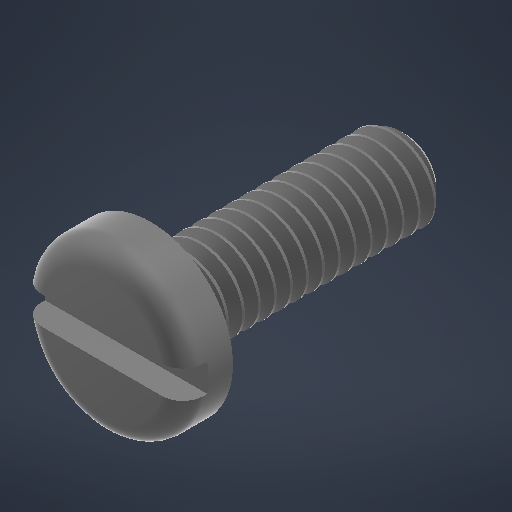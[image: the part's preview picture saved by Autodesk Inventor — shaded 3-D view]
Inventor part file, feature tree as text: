
AUTODESK INVENTOR PART (.ipt)
format: ipt  version: 2025.2 (Build 292293000, 293)  size: 487,424 bytes
history: native  units: in
note: dims shown in document units (in); Inventor stores cm internally (conversion verified against a paired STEP export)
features: other x1, extrude x1
ambient origin geometry x8: Origin, YZ Plane, XZ Plane, XY Plane, X Axis, Y Axis, Z Axis, Center Point
bodies: Solid1 (feature_tree)
feature tree (2):
  other  "Plane1"
  extrude  "Extrude15"  [1 undecoded]
note: 1 required parameter value undecoded (feature->parameter linkage not recoverable at this tier; creation-order binding heuristic only, values carry confidence <= 0.55)
